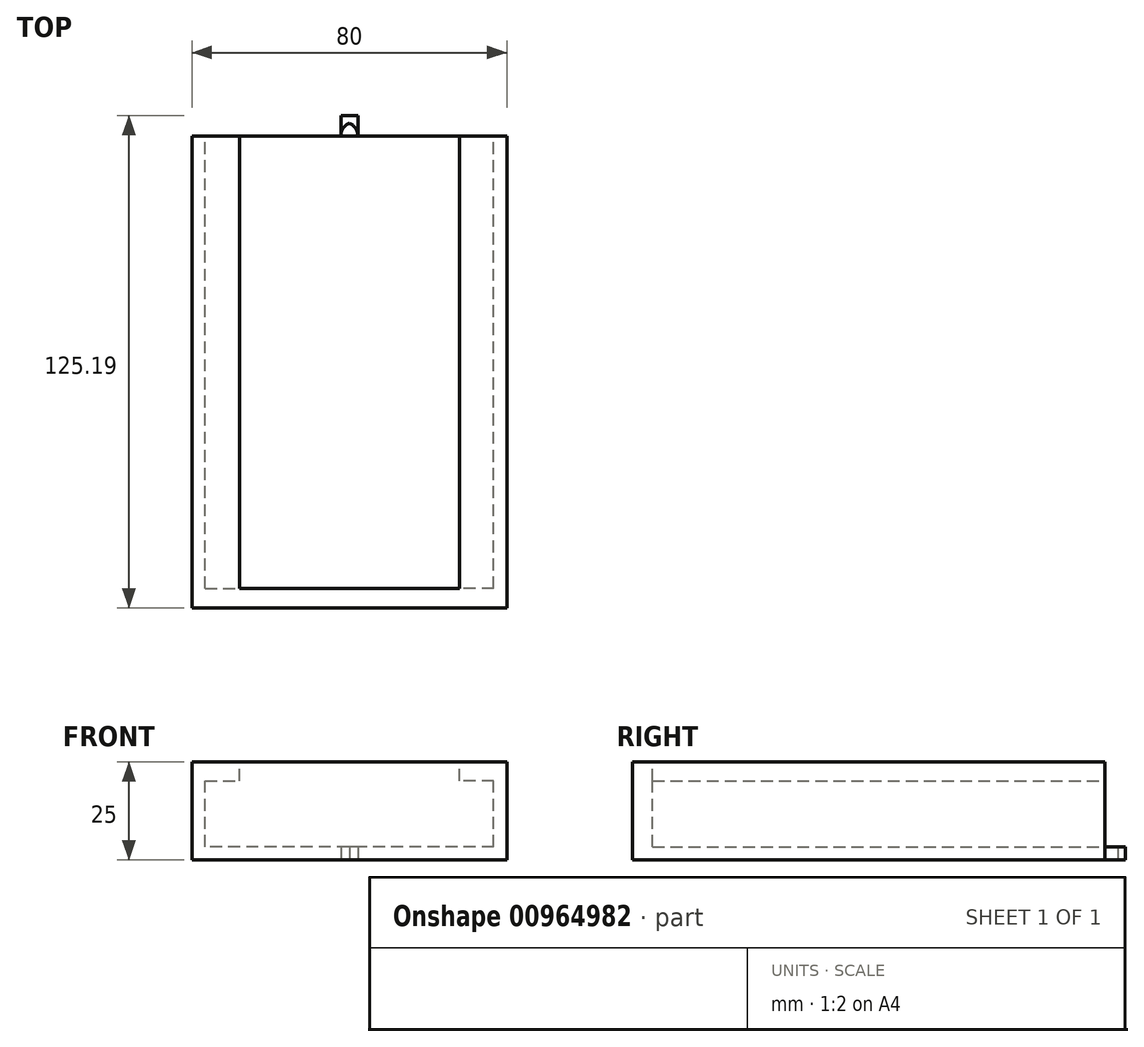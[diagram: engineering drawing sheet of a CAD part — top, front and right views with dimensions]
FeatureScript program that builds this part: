
annotation { "Feature Type Name" : "Feature", "Feature Type Description" : "" }
export const myFeature = defineFeature(function(context is Context, id is Id, definition is map)
    precondition{}
    {
        {
            var Q0;
            Q0=qCreatedBy(makeId("Top.planeOp"),FACE);
            var sketch = newSketch(context, id + "F0", { "sketchPlane" : qUnion([Q0])});
            skLineSegment(sketch, "E0.bottom", {"start": v(40, 60) * mm, "end": v(-40, 60) * mm});
            skLineSegment(sketch, "E0.top", {"start": v(40, -60) * mm, "end": v(-40, -60) * mm});
            skLineSegment(sketch, "E0.left", {"start": v(40, 60) * mm, "end": v(40, -60) * mm});
            skLineSegment(sketch, "E0.right", {"start": v(-40, 60) * mm, "end": v(-40, -60) * mm});
            skPoint(sketch, "E0.middle", {"position": v(0, 0) * mm});
            skSolve(sketch);
        }
        {
            var Q0;
            Q0=makeQuery(id+"F0.imprint","IMPRINT",FACE,{"disambiguationData":[TD([[makeQuery(id+"F0.imprint","IMPRINT",EDGE,{"derivedFrom":sQuery(id+"F0.wireOp",EDGE,"E0.bottom")}),1.0]])]});
            extrude(context, id + "F1", {"entities" : qUnion([Q0]), "depth" : 25 * mm, "offsetDistance" : 25 * mm});
        }
        {
            var Q0;
            Q0=makeQuery(id+"F1.opExtrude","SWEPT_FACE",FACE,{"disambiguationData":[OSD([sQuery(id+"F0.wireOp",EDGE,"E0.bottom")])]});
            var sketch = newSketch(context, id + "F2", { "sketchPlane" : qUnion([Q0])});
            skLineSegment(sketch, "E1", {"start": v(36.65, 3.35) * mm, "end": v(36.65, 20.16) * mm});
            skLineSegment(sketch, "E2", {"start": v(36.65, 20.16) * mm, "end": v(27.94, 20.16) * mm});
            skLineSegment(sketch, "E3", {"start": v(27.94, 20.16) * mm, "end": v(27.94, 25) * mm});
            skLineSegment(sketch, "E4", {"start": v(27.94, 25) * mm, "end": v(0, 25) * mm});
            skLineSegment(sketch, "E5", {"start": v(36.65, 3.35) * mm, "end": v(0, 3.35) * mm});
            skPoint(sketch, "E5.endSnap0", {"position": v(0, 0) * mm});
            skLineSegment(sketch, "E6.MirrorCS", {"start": v(-36.65, 3.35) * mm, "end": v(0, 3.35) * mm});
            skLineSegment(sketch, "E7.MirrorCS", {"start": v(-36.65, 20.16) * mm, "end": v(-27.94, 20.16) * mm});
            skLineSegment(sketch, "E8.MirrorCS", {"start": v(-36.65, 3.35) * mm, "end": v(-36.65, 20.16) * mm});
            skLineSegment(sketch, "E9.MirrorCS", {"start": v(-27.94, 20.16) * mm, "end": v(-27.94, 25) * mm});
            skLineSegment(sketch, "E10.MirrorCS", {"start": v(-27.94, 25) * mm, "end": v(0, 25) * mm});
            skSolve(sketch);
        }
        {
            var Q0;
            Q0 = qSketchRegion(id + "F2", true);
            extrude(context, id + "F3", {"entities" : qUnion([Q0]), "operationType" : NewBodyOperationType.REMOVE, "oppositeDirection" : true, "depth" : 115 * mm, "offsetDistance" : 25 * mm});
        }
        {
            var Q0;
            Q0=makeQuery(id+"F0.imprint","IMPRINT",FACE,{"disambiguationData":[TD([[makeQuery(id+"F0.imprint","IMPRINT",EDGE,{"derivedFrom":sQuery(id+"F0.wireOp",EDGE,"E0.bottom")}),1.0]])]});
            var sketch = newSketch(context, id + "F4", { "sketchPlane" : qUnion([Q0])});
            skPoint(sketch, "E11.end.orphan", {"position": v(0, 67.6) * mm});
            skLineSegment(sketch, "E12", {"start": v(2.16, 60) * mm, "end": v(2.16, 65.2) * mm});
            skLineSegment(sketch, "E13", {"start": v(2.16, 65.2) * mm, "end": v(0, 65.2) * mm});
            skArc(sketch, "E14", {"start": v(2.16, 60) * mm, "mid": v(1.57, 61.94) * mm, "end": v(0, 63.22) * mm});
            skArc(sketch, "E15.MirrorCS", {"start": v(-2.16, 60) * mm, "mid": v(-1.57, 61.94) * mm, "end": v(0, 63.22) * mm});
            skLineSegment(sketch, "E16.MirrorCS", {"start": v(-2.16, 60) * mm, "end": v(-2.16, 65.2) * mm});
            skLineSegment(sketch, "E17.MirrorCS", {"start": v(-2.16, 65.2) * mm, "end": v(0, 65.2) * mm});
            skSolve(sketch);
        }
        {
            var Q0;
            Q0=makeQuery(id+"F4.imprint","IMPRINT",FACE,{"disambiguationData":[TD([[makeQuery(id+"F4.imprint","IMPRINT",EDGE,{"derivedFrom":sQuery(id+"F4.wireOp",EDGE,"E12")}),1.0]])]});
            extrude(context, id + "F5", {"entities" : qUnion([Q0]), "depth" : 3.4 * mm, "offsetDistance" : 25 * mm});
        }
    });
